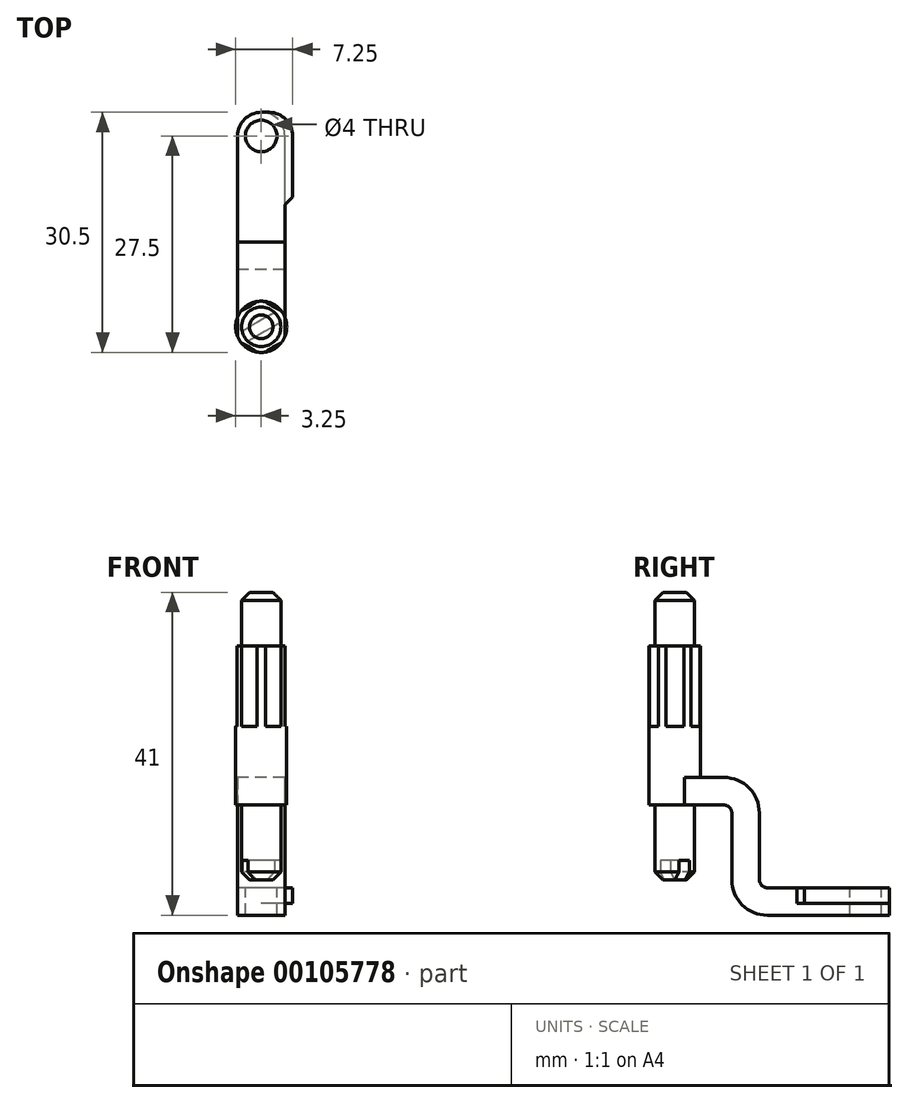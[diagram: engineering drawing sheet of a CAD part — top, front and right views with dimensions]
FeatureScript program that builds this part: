
annotation { "Feature Type Name" : "Feature", "Feature Type Description" : "" }
export const myFeature = defineFeature(function(context is Context, id is Id, definition is map)
    precondition{}
    {
        {
            var Q0;
            Q0=qCreatedBy(makeId("Top.planeOp"),FACE);
            var sketch = newSketch(context, id + "F0", { "sketchPlane" : qUnion([Q0])});
            skCircle(sketch, "E0", {"center": v(0, 0) * mm, "radius": 2.5 * mm});
            skSolve(sketch);
        }
        {
            var Q0;
            Q0=makeQuery(id+"F0.imprint","IMPRINT",FACE,{"disambiguationData":[TD([[makeQuery(id+"F0.imprint","IMPRINT",EDGE,{"derivedFrom":sQuery(id+"F0.wireOp",EDGE,"E0")}),1.0]])]});
            extrude(context, id + "F1", {"entities" : qUnion([Q0]), "depth" : 36.5 * mm});
        }
        {
            var Q0;
            Q0=qCreatedBy(makeId("Top.planeOp"),FACE);
            var sketch = newSketch(context, id + "F2", { "sketchPlane" : qUnion([Q0])});
            skCircle(sketch, "E1", {"center": v(0, 0) * mm, "radius": 3.25 * mm});
            skSolve(sketch);
        }
        {
            var Q0;
            Q0=makeQuery(id+"F2.imprint","IMPRINT",FACE,{"disambiguationData":[TD([[makeQuery(id+"F2.imprint","IMPRINT",EDGE,{"derivedFrom":sQuery(id+"F2.wireOp",EDGE,"E1")}),1.0]])]});
            extrude(context, id + "F3", {"entities" : qUnion([Q0]), "operationType" : NewBodyOperationType.ADD, "depth" : 19.5 * mm, "hasSecondDirection" : true, "secondDirectionOppositeDirection" : false, "secondDirectionDepth" : 9.5 * mm});
        }
        {
            var Q0;
            Q0=qCreatedBy(makeId("Right.planeOp"),FACE);
            var sketch = newSketch(context, id + "F4", { "sketchPlane" : qUnion([Q0])});
            skLineSegment(sketch, "E2", {"start": v(0, 9.5) * mm, "end": v(6.25, 9.5) * mm});
            skLineSegment(sketch, "E3", {"start": v(7.25, 8.5) * mm, "end": v(7.25, 0) * mm});
            skLineSegment(sketch, "E4", {"start": v(11.75, -4.5) * mm, "end": v(27.25, -4.5) * mm});
            skLineSegment(sketch, "E5.0", {"start": v(11.75, -1) * mm, "end": v(27.25, -1) * mm});
            skLineSegment(sketch, "E5.1", {"start": v(10.75, 8.5) * mm, "end": v(10.75, 0) * mm});
            skLineSegment(sketch, "E5.2", {"start": v(0, 13) * mm, "end": v(6.25, 13) * mm});
            skLineSegment(sketch, "E6.0", {"start": v(-3.25, 9.5) * mm, "end": v(3.25, 9.5) * mm, "construction": true});
            skLineSegment(sketch, "E7", {"start": v(0, 9.5) * mm, "end": v(0, 13) * mm});
            skPoint(sketch, "E8.visualSharp", {"position": v(7.25, 9.5) * mm});
            skArc(sketch, "E8.filletArc", {"start": v(7.25, 8.5) * mm, "mid": v(6.96, 9.2) * mm, "end": v(6.25, 9.5) * mm});
            skPoint(sketch, "E9.visualSharp", {"position": v(10.75, -1) * mm});
            skArc(sketch, "E9.filletArc", {"start": v(10.75, 0) * mm, "mid": v(11.04, -0.7) * mm, "end": v(11.75, -1) * mm});
            skPoint(sketch, "E10.visualSharp", {"position": v(7.25, -4.5) * mm});
            skArc(sketch, "E10.filletArc", {"start": v(7.25, 0) * mm, "mid": v(8.57, -3.18) * mm, "end": v(11.75, -4.5) * mm});
            skPoint(sketch, "E11.visualSharp", {"position": v(10.75, 13) * mm});
            skArc(sketch, "E11.filletArc", {"start": v(10.75, 8.5) * mm, "mid": v(9.43, 11.68) * mm, "end": v(6.25, 13) * mm});
            skLineSegment(sketch, "E12", {"start": v(27.25, -4.5) * mm, "end": v(27.25, -1) * mm});
            skSolve(sketch);
        }
        {
            var Q0;
            Q0=makeQuery(id+"F4.imprint","IMPRINT",FACE,{"disambiguationData":[TD([[makeQuery(id+"F4.imprint","IMPRINT",EDGE,{"derivedFrom":sQuery(id+"F4.wireOp",EDGE,"E2")}),1.0]])]});
            extrude(context, id + "F5", {"entities" : qUnion([Q0]), "endBound" : BoundingType.SYMMETRIC, "depth" : 6 * mm});
        }
        {
            var Q0;
            Q0=makeQuery(id+"F1.opExtrude","CAP_FACE",FACE,{"disambiguationData":[OSD([sQuery(id+"F0.wireOp",EDGE,"E0")])],"isStart":false});
            var sketch = newSketch(context, id + "F6", { "sketchPlane" : qUnion([Q0])});
            skArc(sketch, "E13.0", {"start": v(3.04, 1.14) * mm, "mid": v(2.81, 1.62) * mm, "end": v(2.5, 2.07) * mm});
            skArc(sketch, "E14", {"start": v(3.04, 1.14) * mm, "mid": v(3, 0) * mm, "end": v(3.04, -1.14) * mm});
            skCircle(sketch, "E15", {"center": v(0, 0) * mm, "radius": 3 * mm, "construction": true});
            skArc(sketch, "E16.1.0", {"start": v(0.53, 3.2) * mm, "mid": v(1.5, 2.6) * mm, "end": v(2.5, 2.07) * mm});
            skArc(sketch, "E16.2.0", {"start": v(-2.5, 2.07) * mm, "mid": v(-1.5, 2.6) * mm, "end": v(-0.53, 3.2) * mm});
            skArc(sketch, "E16.3.0", {"start": v(-3.04, -1.14) * mm, "mid": v(-3, 0) * mm, "end": v(-3.04, 1.14) * mm});
            skArc(sketch, "E16.4.0", {"start": v(-0.53, -3.2) * mm, "mid": v(-1.5, -2.6) * mm, "end": v(-2.5, -2.07) * mm});
            skArc(sketch, "E16.5.0", {"start": v(2.5, -2.07) * mm, "mid": v(1.5, -2.6) * mm, "end": v(0.53, -3.2) * mm});
            skArc(sketch, "E17.trimOffspring", {"start": v(-0.53, -3.2) * mm, "mid": v(0, -3.25) * mm, "end": v(0.53, -3.2) * mm});
            skArc(sketch, "E18.trimOffspring", {"start": v(-3.04, -1.14) * mm, "mid": v(-2.81, -1.62) * mm, "end": v(-2.5, -2.07) * mm});
            skArc(sketch, "E19.trimOffspring", {"start": v(-2.5, 2.07) * mm, "mid": v(-2.81, 1.63) * mm, "end": v(-3.04, 1.14) * mm});
            skArc(sketch, "E20.trimOffspring", {"start": v(0.53, 3.2) * mm, "mid": v(0, 3.25) * mm, "end": v(-0.53, 3.2) * mm});
            skArc(sketch, "E21.trimOffspring", {"start": v(2.5, -2.07) * mm, "mid": v(2.81, -1.63) * mm, "end": v(3.04, -1.14) * mm});
            skSolve(sketch);
        }
        {
            var Q0;
            Q0 = qSketchRegion(id + "F6", true);
            extrude(context, id + "F7", {"entities" : qUnion([Q0]), "operationType" : NewBodyOperationType.ADD, "oppositeDirection" : true, "depth" : 25 * mm, "hasSecondDirection" : true, "secondDirectionOppositeDirection" : true, "secondDirectionDepth" : 6.8 * mm});
        }
        {
            var Q0;
            Q0=makeQuery(id+"F5.opExtrude","SWEPT_FACE",FACE,{"disambiguationData":[OSD([sQuery(id+"F4.wireOp",EDGE,"E5.0")])]});
            var sketch = newSketch(context, id + "F8", { "sketchPlane" : qUnion([Q0])});
            skCircle(sketch, "E22", {"center": v(0, 24.25) * mm, "radius": 2 * mm});
            skPoint(sketch, "E22.centerSnap0", {"position": v(0, 27.25) * mm});
            skSolve(sketch);
        }
        {
            var Q0;
            Q0 = qSketchRegion(id + "F8", true);
            extrude(context, id + "F9", {"entities" : qUnion([Q0]), "operationType" : NewBodyOperationType.REMOVE, "endBound" : BoundingType.THROUGH_ALL, "oppositeDirection" : true, "depth" : 25 * mm});
        }
        {
            var Q0;
            Q0=makeQuery(id+"F5.opExtrude","CAP_EDGE",EDGE,{"disambiguationData":[OSD([sQuery(id+"F4.wireOp",EDGE,"E12")])],"isStart":true});
            var Q1;
            Q1=makeQuery(id+"F5.opExtrude","CAP_EDGE",EDGE,{"disambiguationData":[OSD([sQuery(id+"F4.wireOp",EDGE,"E12")])],"isStart":false});
            fillet(context, id + "F10", {"entities" : qUnion([Q0, Q1]), "radius" : 3 * mm, "tangentPropagation" : true, "allowEdgeOverflow" : false});
        }
        {
            var Q0;
            Q0=makeQuery(id+"F1.opExtrude","CAP_FACE",FACE,{"disambiguationData":[OSD([sQuery(id+"F0.wireOp",EDGE,"E0")])],"isStart":true});
            var sketch = newSketch(context, id + "F11", { "sketchPlane" : qUnion([Q0])});
            skLineSegment(sketch, "E23", {"start": v(2.44, -0.54) * mm, "end": v(-1.7, 1.84) * mm});
            skLineSegment(sketch, "E24", {"start": v(1.7, -1.84) * mm, "end": v(-2.44, 0.54) * mm});
            skCircle(sketch, "E25", {"center": v(0, 0) * mm, "radius": 0.75 * mm, "construction": true});
            skArc(sketch, "E26", {"start": v(-1.7, 1.84) * mm, "mid": v(-2.17, 1.25) * mm, "end": v(-2.44, 0.54) * mm});
            skArc(sketch, "E27.trimOffspring", {"start": v(1.7, -1.84) * mm, "mid": v(2.17, -1.25) * mm, "end": v(2.44, -0.54) * mm});
            skSolve(sketch);
        }
        {
            var Q0;
            Q0 = qSketchRegion(id + "F11", true);
            extrude(context, id + "F12", {"entities" : qUnion([Q0]), "operationType" : NewBodyOperationType.REMOVE, "oppositeDirection" : true, "depth" : 2.5 * mm});
        }
        {
            var Q0;
            {var subQ0=sQuery(id+"F0.wireOp",EDGE,"E0");Q0=makeQuery(id+"F12.boolean.opBoolean","SPLIT",EDGE,{"disambiguationData":[TD([makeQuery(id+"F12.opExtrude","SWEPT_FACE",FACE,{"disambiguationData":[OSD([sQuery(id+"F11.wireOp",EDGE,"E23")])]})])],"derivedFrom":makeQuery(id+"F1.opExtrude","CAP_EDGE",EDGE,{"disambiguationData":[OSD([subQ0])],"isStart":true})});}
            var Q1;
            {var subQ0=sQuery(id+"F0.wireOp",EDGE,"E0");Q1=makeQuery(id+"F12.boolean.opBoolean","SPLIT",EDGE,{"disambiguationData":[TD([makeQuery(id+"F12.opExtrude","SWEPT_FACE",FACE,{"disambiguationData":[OSD([sQuery(id+"F11.wireOp",EDGE,"E24")])]})])],"derivedFrom":makeQuery(id+"F1.opExtrude","CAP_EDGE",EDGE,{"disambiguationData":[OSD([subQ0])],"isStart":true})});}
            var Q2;
            Q2=makeQuery(id+"F1.opExtrude","CAP_EDGE",EDGE,{"disambiguationData":[OSD([sQuery(id+"F0.wireOp",EDGE,"E0")])],"isStart":false});
            chamfer(context, id + "F13", {"entities" : qUnion([Q0, Q1, Q2]), "width" : 1 * mm, "tangentPropagation" : true});
        }
        {
            var Q0;
            Q0=makeQuery(id+"F5.opExtrude","SWEPT_FACE",FACE,{"disambiguationData":[OSD([sQuery(id+"F4.wireOp",EDGE,"E5.0")])]});
            var sketch = newSketch(context, id + "F14", { "sketchPlane" : qUnion([Q0])});
            skLineSegment(sketch, "E28", {"start": v(3, 15.5) * mm, "end": v(4, 16.5) * mm});
            skLineSegment(sketch, "E29", {"start": v(4, 16.5) * mm, "end": v(4, 24.25) * mm});
            skLineSegment(sketch, "E30", {"start": v(1, 27.25) * mm, "end": v(0, 27.25) * mm});
            skPoint(sketch, "E31.visualSharp", {"position": v(4, 27.25) * mm});
            skArc(sketch, "E31.filletArc", {"start": v(4, 24.25) * mm, "mid": v(3.12, 26.37) * mm, "end": v(1, 27.25) * mm});
            skLineSegment(sketch, "E32.0", {"start": v(3, 15.5) * mm, "end": v(3, 24.25) * mm});
            skArc(sketch, "E33.0", {"start": v(3, 24.25) * mm, "mid": v(2.12, 26.37) * mm, "end": v(0, 27.25) * mm});
            skPoint(sketch, "E34.orphan", {"position": v(-3, 24.25) * mm});
            skPoint(sketch, "E35.orphan", {"position": v(3, 11.75) * mm});
            skSolve(sketch);
        }
        {
            var Q0;
            Q0 = qSketchRegion(id + "F14", true);
            extrude(context, id + "F15", {"entities" : qUnion([Q0]), "operationType" : NewBodyOperationType.ADD, "oppositeDirection" : true, "depth" : 2 * mm});
        }
    });
